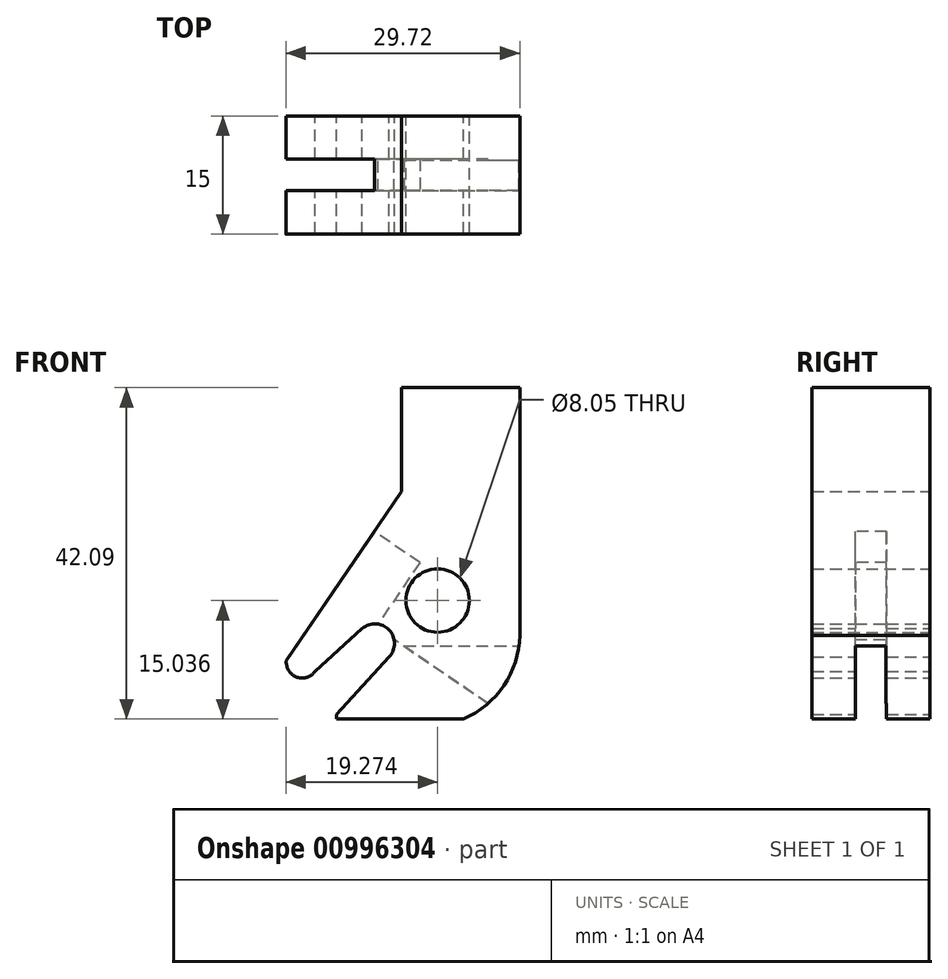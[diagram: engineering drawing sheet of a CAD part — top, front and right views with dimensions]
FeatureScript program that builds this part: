
annotation { "Feature Type Name" : "Feature", "Feature Type Description" : "" }
export const myFeature = defineFeature(function(context is Context, id is Id, definition is map)
    precondition{}
    {
        {
            var Q0;
            Q0=qCreatedBy(makeId("Front.planeOp"),FACE);
            var sketch = newSketch(context, id + "F0", { "sketchPlane" : qUnion([Q0])});
            skLineSegment(sketch, "E0.bottom", {"start": v(15, 20) * mm, "end": v(0, 20) * mm});
            skLineSegment(sketch, "E0.left", {"start": v(15, 20) * mm, "end": v(15, -11.48) * mm});
            skPoint(sketch, "E0.middle", {"position": v(0, 0) * mm});
            skCircle(sketch, "E1", {"center": v(4.55, -7.05) * mm, "radius": 4.03 * mm});
            skArc(sketch, "E2", {"start": v(-1.6, -14.2) * mm, "mid": v(-1.6, -10.78) * mm, "end": v(-5.03, -10.59) * mm});
            skLineSegment(sketch, "E3", {"start": v(0, 20) * mm, "end": v(0, 6.82) * mm});
            skLineSegment(sketch, "E4", {"start": v(-8.3, -22.09) * mm, "end": v(7.82, -22.09) * mm});
            skLineSegment(sketch, "E5", {"start": v(-8.3, -22.09) * mm, "end": v(-8.3, -21.53) * mm});
            skLineSegment(sketch, "E6", {"start": v(0, 6.82) * mm, "end": v(-14.67, -14.71) * mm});
            skLineSegment(sketch, "E7", {"start": v(-14.7, -14.95) * mm, "end": v(-14.58, -15.42) * mm});
            skPoint(sketch, "E8.visualSharp", {"position": v(-14.74, -14.82) * mm});
            skArc(sketch, "E8.filletArc", {"start": v(-14.67, -14.71) * mm, "mid": v(-14.71, -14.83) * mm, "end": v(-14.7, -14.95) * mm});
            skArc(sketch, "E9.filletArc", {"start": v(-14.58, -15.42) * mm, "mid": v(-13, -16.87) * mm, "end": v(-11.03, -16.07) * mm});
            skArc(sketch, "E10", {"start": v(-8.3, -21.53) * mm, "mid": v(-8.32, -21.8) * mm, "end": v(-8.3, -22.09) * mm});
            skLineSegment(sketch, "E11", {"start": v(-11.03, -16.07) * mm, "end": v(-5.03, -10.59) * mm});
            skLineSegment(sketch, "E12", {"start": v(-8.3, -21.53) * mm, "end": v(-1.6, -14.2) * mm});
            skArc(sketch, "E13", {"start": v(7.82, -22.09) * mm, "mid": v(13.1, -17.68) * mm, "end": v(15, -11.07) * mm});
            skSolve(sketch);
        }
        {
            var Q0;
            Q0=makeQuery(id+"F0.imprint","IMPRINT",FACE,{"disambiguationData":[TD([[makeQuery(id+"F0.imprint","IMPRINT",EDGE,{"derivedFrom":sQuery(id+"F0.wireOp",EDGE,"E0.bottom")}),1.0]])]});
            extrude(context, id + "F1", {"entities" : qUnion([Q0]), "depth" : 15 * mm, "offsetDistance" : 25 * mm});
        }
        {
            var Q0;
            Q0=makeQuery(id+"F1.opExtrude","SWEPT_FACE",FACE,{"disambiguationData":[OSD([sQuery(id+"F0.wireOp",EDGE,"E6")])]});
            var sketch = newSketch(context, id + "F2", { "sketchPlane" : qUnion([Q0])});
            skLineSegment(sketch, "E14", {"start": v(9.5, -29.26) * mm, "end": v(5.5, -29.26) * mm});
            skLineSegment(sketch, "E15", {"start": v(5.5, -10.45) * mm, "end": v(5.5, -29.26) * mm});
            skLineSegment(sketch, "E16", {"start": v(9.5, -29.26) * mm, "end": v(9.5, -10.45) * mm});
            skLineSegment(sketch, "E17", {"start": v(5.5, -10.45) * mm, "end": v(9.5, -10.45) * mm});
            skSolve(sketch);
        }
        {
            var Q0;
            {var subQ0=sQuery(id+"F2.wireOp",EDGE,"E14");Q0=makeQuery(id+"F2.imprint","IMPRINT",FACE,{"disambiguationData":[TD([[makeQuery(id+"F2.imprint","IMPRINT",EDGE,{"derivedFrom":subQ0}),-1.0]])]});}
            var Q1;
            {var subQ0=sQuery(id+"F2.wireOp",EDGE,"E17");Q1=makeQuery(id+"F2.imprint","IMPRINT",FACE,{"disambiguationData":[TD([[makeQuery(id+"F2.imprint","IMPRINT",EDGE,{"derivedFrom":subQ0}),-1.0]])]});}
            extrude(context, id + "F3", {"entities" : qUnion([Q0, Q1]), "operationType" : NewBodyOperationType.REMOVE, "endBound" : BoundingType.THROUGH_ALL, "oppositeDirection" : true, "depth" : 25 * mm, "offsetDistance" : 25 * mm});
        }
        {
            var Q0;
            Q0=makeQuery(id+"F1.opExtrude","SWEPT_FACE",FACE,{"disambiguationData":[OSD([sQuery(id+"F0.wireOp",EDGE,"E6")])]});
            var sketch = newSketch(context, id + "F4", { "sketchPlane" : qUnion([Q0])});
            skLineSegment(sketch, "E18", {"start": v(5.5, -10.45) * mm, "end": v(5.5, -0.55) * mm});
            skLineSegment(sketch, "E19", {"start": v(5.5, -0.55) * mm, "end": v(9.5, -0.55) * mm});
            skLineSegment(sketch, "E20", {"start": v(9.5, -0.55) * mm, "end": v(9.5, -10.45) * mm});
            skSolve(sketch);
        }
        {
            var Q0;
            Q0=makeQuery(id+"F4.imprint","IMPRINT",FACE,{"disambiguationData":[TD([[makeQuery(id+"F4.imprint","IMPRINT",EDGE,{"derivedFrom":sQuery(id+"F4.wireOp",EDGE,"E18")}),-1.0]])]});
            var Q1;
            Q1=makeQuery(id+"F1.opExtrude","SWEPT_FACE",FACE,{"disambiguationData":[OSD([sQuery(id+"F0.wireOp",EDGE,"E1")])]});
            extrude(context, id + "F5", {"entities" : qUnion([Q0]), "operationType" : NewBodyOperationType.REMOVE, "oppositeDirection" : true, "depth" : 7 * mm, "endBoundEntityFace" : qUnion([Q1]), "offsetDistance" : 25 * mm});
        }
        {
            var Q0;
            Q0=makeQuery(id+"F1.opExtrude","SWEPT_FACE",FACE,{"disambiguationData":[OSD([sQuery(id+"F0.wireOp",EDGE,"E0.left")])]});
            var sketch = newSketch(context, id + "F6", { "sketchPlane" : qUnion([Q0])});
            skLineSegment(sketch, "E21", {"start": v(-9.47, -22.09) * mm, "end": v(-9.47, -16.31) * mm});
            skLineSegment(sketch, "E22", {"start": v(-5.6, -16.31) * mm, "end": v(-5.6, -22.09) * mm});
            skLineSegment(sketch, "E23", {"start": v(-9.47, -22.09) * mm, "end": v(-5.6, -22.09) * mm});
            skLineSegment(sketch, "E24", {"start": v(-9.47, -16.31) * mm, "end": v(-9.47, -12.84) * mm});
            skLineSegment(sketch, "E25", {"start": v(-9.47, -12.84) * mm, "end": v(-5.6, -12.84) * mm});
            skLineSegment(sketch, "E26", {"start": v(-5.6, -12.84) * mm, "end": v(-5.6, -16.31) * mm});
            skSolve(sketch);
        }
        {
            var Q0;
            {var subQ0=sQuery(id+"F6.wireOp",EDGE,"E23");Q0=makeQuery(id+"F6.imprint","IMPRINT",FACE,{"disambiguationData":[TD([[makeQuery(id+"F6.imprint","IMPRINT",EDGE,{"derivedFrom":subQ0}),1.0]])]});}
            var Q1;
            {var subQ0=sQuery(id+"F6.wireOp",EDGE,"KIqVmMam-SnmZ-E4L6-Me5D-dZEmiyJ8HNY7");Q1=makeQuery(id+"F6.imprint","IMPRINT",FACE,{"disambiguationData":[TD([[makeQuery(id+"F6.imprint","IMPRINT",EDGE,{"derivedFrom":subQ0}),-1.0]])]});}
            extrude(context, id + "F7", {"entities" : qUnion([Q0, Q1]), "operationType" : NewBodyOperationType.REMOVE, "endBound" : BoundingType.THROUGH_ALL, "oppositeDirection" : true, "depth" : 25 * mm, "offsetDistance" : 25 * mm});
        }
    });
